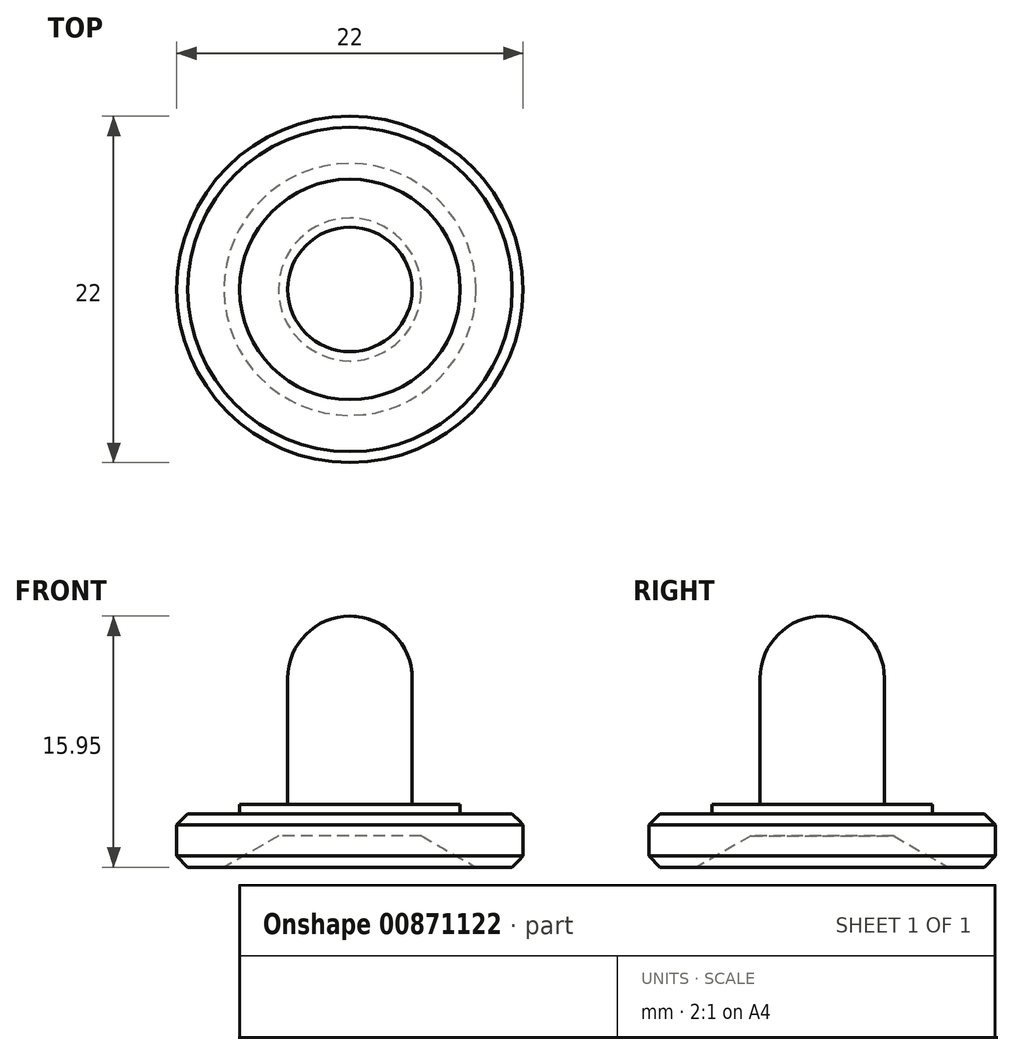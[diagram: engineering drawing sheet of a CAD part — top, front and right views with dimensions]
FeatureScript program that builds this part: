
annotation { "Feature Type Name" : "Feature", "Feature Type Description" : "" }
export const myFeature = defineFeature(function(context is Context, id is Id, definition is map)
    precondition{}
    {
        {
            var Q0;
            Q0=qCreatedBy(makeId("Front.planeOp"),FACE);
            var sketch = newSketch(context, id + "F0", { "sketchPlane" : qUnion([Q0])});
            skLineSegment(sketch, "E0", {"start": v(0, 2) * mm, "end": v(4.54, 2) * mm});
            skLineSegment(sketch, "E1", {"start": v(4.54, 2) * mm, "end": v(8, 0) * mm});
            skLineSegment(sketch, "E2", {"start": v(8, 0) * mm, "end": v(11, 0) * mm});
            skLineSegment(sketch, "E3", {"start": v(11, 0) * mm, "end": v(11, 3.4) * mm});
            skLineSegment(sketch, "E4", {"start": v(11, 3.4) * mm, "end": v(7, 3.4) * mm});
            skLineSegment(sketch, "E5", {"start": v(3.95, 4) * mm, "end": v(3.95, 12) * mm});
            skLineSegment(sketch, "E6", {"start": v(3.95, 4) * mm, "end": v(7, 4) * mm});
            skLineSegment(sketch, "E7", {"start": v(7, 4) * mm, "end": v(7, 3.4) * mm});
            skArc(sketch, "E8", {"start": v(3.95, 12) * mm, "mid": v(2.8, 14.8) * mm, "end": v(0, 15.95) * mm});
            skLineSegment(sketch, "E9", {"start": v(0, 15.95) * mm, "end": v(0, 2) * mm});
            skLineSegment(sketch, "E10", {"start": v(10.3, 3.4) * mm, "end": v(11, 2.68) * mm});
            skLineSegment(sketch, "E11", {"start": v(10.3, 0) * mm, "end": v(11, 0.72) * mm});
            skSolve(sketch);
        }
        {
            var Q0;
            Q0=makeQuery(id+"F0.imprint","IMPRINT",FACE,{"disambiguationData":[TD([[makeQuery(id+"F0.imprint","IMPRINT",EDGE,{"derivedFrom":sQuery(id+"F0.wireOp",EDGE,"E0")}),1.0]])]});
            var Q1;
            Q1=sQuery(id+"F0.wireOp",EDGE,"E9");
            revolve(context, id + "F1", {"surfaceOperationType" : NewSurfaceOperationType.NEW, "entities" : qUnion([Q0]), "axis" : qUnion([Q1]), "revolveType" : RevolveType.FULL});
        }
    });
